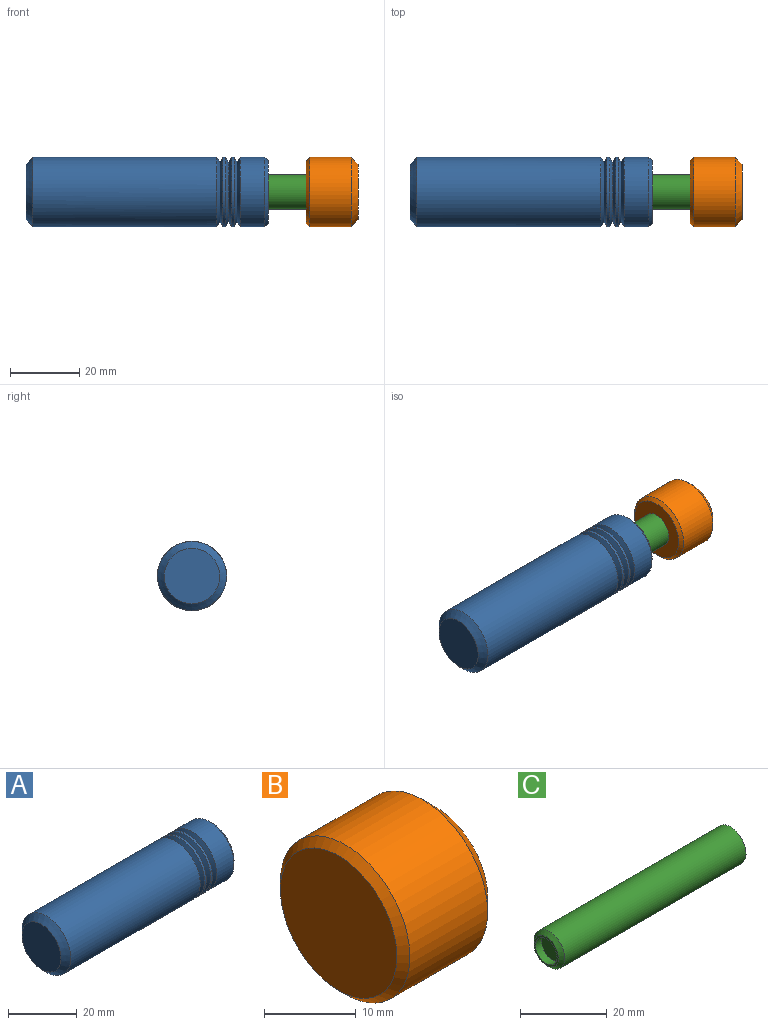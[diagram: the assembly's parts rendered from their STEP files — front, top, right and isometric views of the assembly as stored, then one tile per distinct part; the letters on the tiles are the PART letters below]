
ASSEMBLY  parts=3 mates=2
PART A: 17 faces, bbox 70x20x20 mm
  f0: cylinder r=10mm len=20mm, axis (-1,0,0), area 48.3mm2, adj f11,f12
  f1: cylinder r=10mm len=20mm, axis (-1,0,0), area 48.3mm2, adj f9,f10
  f2: cylinder r=10mm len=20mm, axis (-1,0,0), area 448.2mm2, adj f6,f8
  f3: plane 18x18mm, normal (1,0,0), area 175.9mm2, adj f4,f6
  f4: cylinder r=5mm len=59mm, axis (1,0,0), area 1853.5mm2, adj f3,f7
  f5: plane 8x8mm, normal (1,0,0), area 50.3mm2, adj f7
  f6: cone r=9mm half-angle=45deg, axis (-1,0,0), area 84.4mm2, adj f2,f3
  f7: cone r=4mm half-angle=45deg, axis (1,0,0), area 40mm2, adj f4,f5
  f8: cone r=10.23mm half-angle=60deg, axis (1,0,0), area 100.7mm2, adj f2,f9
  f9: cone r=8.5mm half-angle=60deg, axis (-1,0,0), area 100.7mm2, adj f1,f8
  f10: cone r=10.23mm half-angle=60deg, axis (1,0,0), area 100.7mm2, adj f1,f11
  f11: cone r=8.5mm half-angle=60deg, axis (-1,0,0), area 100.7mm2, adj f0,f10
  f12: cone r=10.23mm half-angle=60deg, axis (1,0,0), area 100.7mm2, adj f0,f13
  f13: cone r=8.5mm half-angle=60deg, axis (-1,0,0), area 100.7mm2, adj f12,f16
  f14: plane 16x16mm, normal (-1,0,0), area 201.1mm2, adj f15
  f15: cone r=10mm half-angle=45deg, axis (1,0,0), area 159.9mm2, adj f14,f16
  f16: cylinder r=10mm len=53.13mm, axis (-1,0,0), area 3338.5mm2, adj f13,f15
PART B: 5 faces, bbox 15x20x20 mm
  f0: cylinder r=10mm len=20mm, axis (-1,0,0), area 754mm2, adj f3,f4
  f1: plane 16x16mm, normal (1,0,0), area 201.1mm2, adj f4
  f2: plane 18x18mm, normal (-1,0,0), area 254.5mm2, adj f3
  f3: cone r=10mm half-angle=45deg, axis (1,0,0), area 84.4mm2, adj f0,f2
  f4: cone r=8mm half-angle=45deg, axis (-1,0,0), area 159.9mm2, adj f0,f1
PART C: 6 faces, bbox 60x10x10 mm
  f0: cylinder r=5mm len=59mm, axis (1,0,0), area 1853.5mm2, adj f2,f3
  f1: plane 8x8mm, normal (-1,0,0), area 11.8mm2, adj f3,f4
  f2: plane 10x10mm, normal (1,0,0), area 78.5mm2, adj f0
  f3: cone r=4mm half-angle=45deg, axis (1,0,0), area 40mm2, adj f0,f1
  f4: cylinder r=3.5mm len=7mm, axis (-1,0,0), area 44mm2, adj f1,f5
  f5: plane 7x7mm, normal (-1,0,0), area 38.5mm2, adj f4
PLACE A at identity fixed
PLACE B t=(10.9,0,0)mm
PLACE C t=(10.9,0,0)mm
MATE fastened C.f0 <-> B.f0  axis (1,0,0) through (45.9,0,0)mm
MATE slider C.f0 <-> A.f4  axis (1,0,0) through (45.9,0,0)mm
